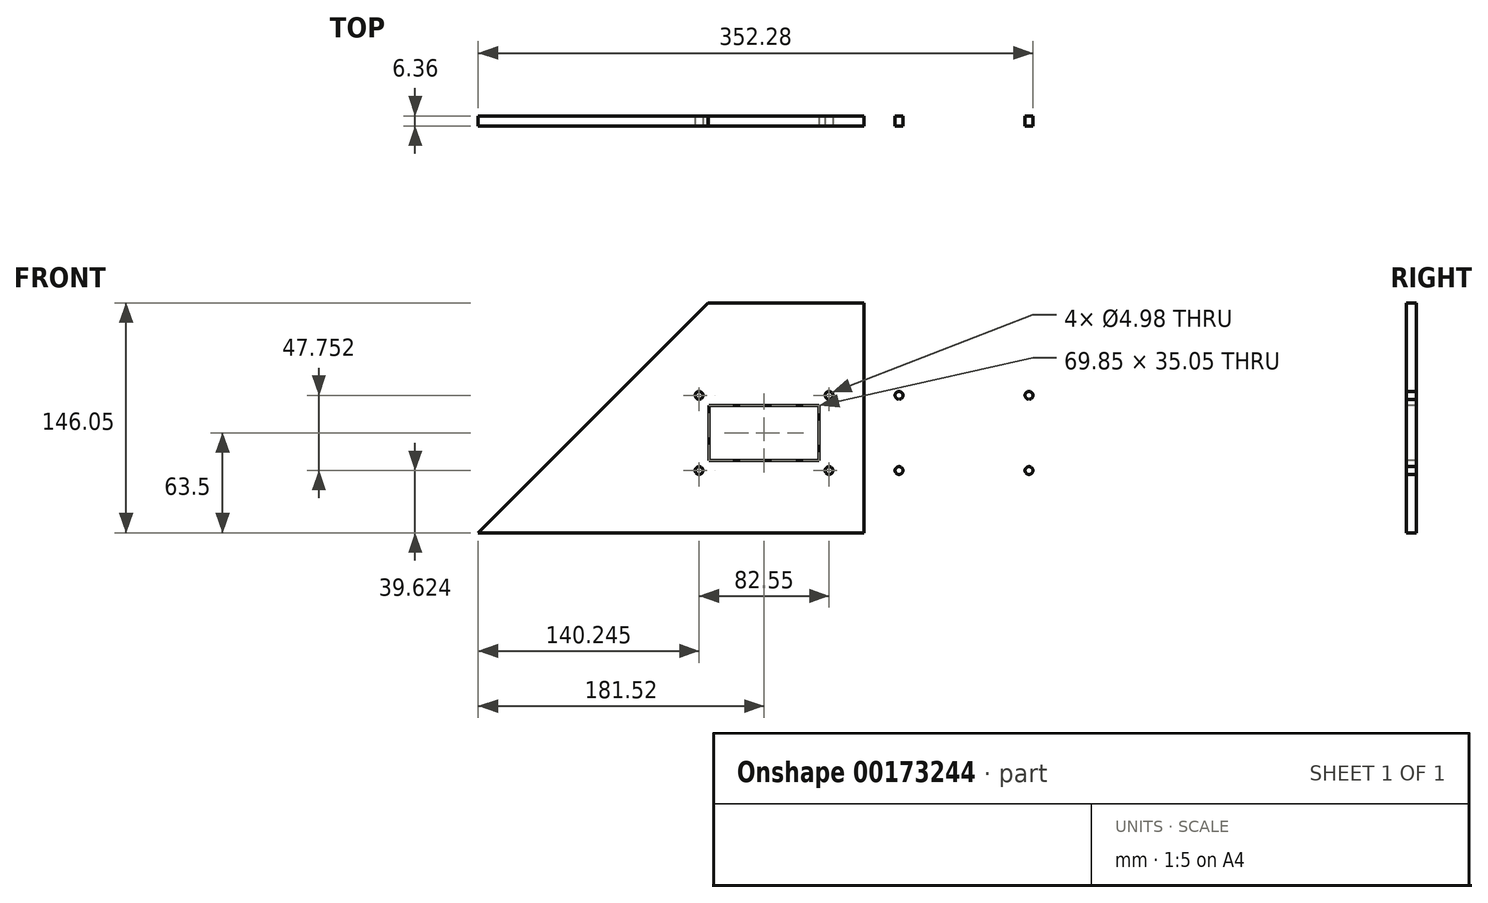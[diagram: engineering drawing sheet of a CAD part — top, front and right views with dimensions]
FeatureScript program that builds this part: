
annotation { "Feature Type Name" : "Feature", "Feature Type Description" : "" }
export const myFeature = defineFeature(function(context is Context, id is Id, definition is map)
    precondition{}
    {
        {
            var Q0;
            Q0=qCreatedBy(makeId("Front.planeOp"),FACE);
            var sketch = newSketch(context, id + "F0", { "sketchPlane" : qUnion([Q0])});
            skLineSegment(sketch, "E0", {"start": v(-98.97, 0) * mm, "end": v(98.97, 0) * mm});
            skLineSegment(sketch, "E1", {"start": v(-98.97, 0) * mm, "end": v(-245.02, -146.05) * mm});
            skLineSegment(sketch, "E2", {"start": v(-245.02, -146.05) * mm, "end": v(245.02, -146.05) * mm});
            skLineSegment(sketch, "E3", {"start": v(245.02, -146.05) * mm, "end": v(98.97, 0) * mm});
            skSolve(sketch);
        }
        {
            var Q0;
            Q0 = qSketchRegion(id + "F0", true);
            extrude(context, id + "F1", {"entities" : qUnion([Q0]), "endBound" : BoundingType.SYMMETRIC, "depth" : 6.35 * mm});
        }
        {
            var Q0;
            Q0=makeQuery(id+"F1.opExtrude","CAP_FACE",FACE,{"disambiguationData":[OSD([sQuery(id+"F0.wireOp",EDGE,"E0"),sQuery(id+"F0.wireOp",EDGE,"E1"),sQuery(id+"F0.wireOp",EDGE,"E2"),sQuery(id+"F0.wireOp",EDGE,"E3")])],"isStart":false});
            var sketch = newSketch(context, id + "F2", { "sketchPlane" : qUnion([Q0])});
            skLineSegment(sketch, "E4", {"start": v(0, 0) * mm, "end": v(0, -146.05) * mm});
            skPoint(sketch, "E5", {"position": v(-63.5, -82.55) * mm});
            skPoint(sketch, "E5.positionSnap0", {"position": v(0, -73.03) * mm});
            skLineSegment(sketch, "E6.bottom", {"start": v(-120.14, -45.09) * mm, "end": v(-6.86, -45.09) * mm});
            skLineSegment(sketch, "E6.top", {"start": v(-120.14, -120.02) * mm, "end": v(-6.86, -120.02) * mm});
            skLineSegment(sketch, "E6.left", {"start": v(-120.14, -45.09) * mm, "end": v(-120.14, -120.02) * mm});
            skLineSegment(sketch, "E6.right", {"start": v(-6.86, -45.09) * mm, "end": v(-6.86, -120.02) * mm});
            skLineSegment(sketch, "E7.bottom", {"start": v(-104.78, -58.67) * mm, "end": v(-22.23, -58.67) * mm});
            skLineSegment(sketch, "E7.top", {"start": v(-104.78, -106.43) * mm, "end": v(-22.23, -106.43) * mm});
            skLineSegment(sketch, "E7.left", {"start": v(-104.78, -58.67) * mm, "end": v(-104.78, -106.43) * mm});
            skLineSegment(sketch, "E7.right", {"start": v(-22.23, -58.67) * mm, "end": v(-22.23, -106.43) * mm});
            skLineSegment(sketch, "E8.bottom", {"start": v(-98.43, -65.02) * mm, "end": v(-28.58, -65.02) * mm});
            skLineSegment(sketch, "E8.top", {"start": v(-98.43, -100.08) * mm, "end": v(-28.58, -100.08) * mm});
            skLineSegment(sketch, "E8.left", {"start": v(-98.43, -65.02) * mm, "end": v(-98.43, -100.08) * mm});
            skLineSegment(sketch, "E8.right", {"start": v(-28.58, -65.02) * mm, "end": v(-28.58, -100.08) * mm});
            skCircle(sketch, "E9", {"center": v(-104.78, -58.67) * mm, "radius": 2.49 * mm});
            skCircle(sketch, "E10", {"center": v(-22.23, -58.67) * mm, "radius": 2.49 * mm});
            skCircle(sketch, "E11", {"center": v(-104.78, -106.43) * mm, "radius": 2.49 * mm});
            skCircle(sketch, "E12", {"center": v(-22.23, -106.43) * mm, "radius": 2.49 * mm});
            skLineSegment(sketch, "E13.MirrorCS", {"start": v(98.43, -65.02) * mm, "end": v(28.58, -65.02) * mm});
            skLineSegment(sketch, "E14.MirrorCS", {"start": v(98.43, -65.02) * mm, "end": v(98.43, -100.08) * mm});
            skLineSegment(sketch, "E15.MirrorCS", {"start": v(28.58, -65.02) * mm, "end": v(28.58, -100.08) * mm});
            skLineSegment(sketch, "E16.MirrorCS", {"start": v(98.43, -100.08) * mm, "end": v(28.58, -100.08) * mm});
            skCircle(sketch, "E17.MirrorC", {"center": v(104.78, -58.67) * mm, "radius": 2.49 * mm});
            skCircle(sketch, "E18.MirrorC", {"center": v(22.23, -58.67) * mm, "radius": 2.49 * mm});
            skCircle(sketch, "E19.MirrorC", {"center": v(22.23, -106.43) * mm, "radius": 2.49 * mm});
            skCircle(sketch, "E20.MirrorC", {"center": v(104.78, -106.43) * mm, "radius": 2.49 * mm});
            skSolve(sketch);
        }
        {
            var Q0;
            Q0=makeQuery(id+"F2.imprint","IMPRINT",FACE,{"disambiguationData":[TD([[makeQuery(id+"F2.imprint","IMPRINT",EDGE,{"derivedFrom":sQuery(id+"F2.wireOp",EDGE,"E13.MirrorCS")}),1.0]])]});
            var Q1;
            Q1=makeQuery(id+"F2.imprint","IMPRINT",FACE,{"disambiguationData":[TD([[makeQuery(id+"F2.imprint","IMPRINT",EDGE,{"derivedFrom":sQuery(id+"F2.wireOp",EDGE,"E17.MirrorC")}),-1.0]])]});
            var Q2;
            Q2=makeQuery(id+"F2.imprint","IMPRINT",FACE,{"disambiguationData":[TD([[makeQuery(id+"F2.imprint","IMPRINT",EDGE,{"derivedFrom":sQuery(id+"F2.wireOp",EDGE,"E18.MirrorC")}),-1.0]])]});
            var Q3;
            Q3=makeQuery(id+"F2.imprint","IMPRINT",FACE,{"disambiguationData":[TD([[makeQuery(id+"F2.imprint","IMPRINT",EDGE,{"derivedFrom":sQuery(id+"F2.wireOp",EDGE,"E19.MirrorC")}),-1.0]])]});
            var Q4;
            Q4=makeQuery(id+"F2.imprint","IMPRINT",FACE,{"disambiguationData":[TD([[makeQuery(id+"F2.imprint","IMPRINT",EDGE,{"derivedFrom":sQuery(id+"F2.wireOp",EDGE,"E20.MirrorC")}),-1.0]])]});
            var Q5;
            {var subQ0=sQuery(id+"F2.wireOp",EDGE,"E7.right");var subQ1=sQuery(id+"F2.wireOp",EDGE,"E7.bottom");var subQ2=makeQuery(id+"F2.imprint","INTERSECT",VERTEX,{"derivedFrom":[subQ1,subQ0]});Q5=makeQuery(id+"F2.imprint","IMPRINT",FACE,{"disambiguationData":[TD([[makeQuery(id+"F2.imprint","IMPRINT",EDGE,{"disambiguationData":[TD([[subQ2,1.0]])],"derivedFrom":subQ1}),1.0]])]});}
            var Q6;
            {var subQ0=sQuery(id+"F2.wireOp",EDGE,"E7.right");var subQ1=sQuery(id+"F2.wireOp",EDGE,"E7.bottom");var subQ2=makeQuery(id+"F2.imprint","INTERSECT",VERTEX,{"derivedFrom":[subQ1,subQ0]});Q6=makeQuery(id+"F2.imprint","IMPRINT",FACE,{"disambiguationData":[TD([[makeQuery(id+"F2.imprint","IMPRINT",EDGE,{"disambiguationData":[TD([[subQ2,1.0]])],"derivedFrom":subQ1}),-1.0]])]});}
            var Q7;
            {var subQ0=sQuery(id+"F2.wireOp",EDGE,"E7.right");var subQ1=sQuery(id+"F2.wireOp",EDGE,"E7.top");var subQ2=makeQuery(id+"F2.imprint","INTERSECT",VERTEX,{"derivedFrom":[subQ1,subQ0]});Q7=makeQuery(id+"F2.imprint","IMPRINT",FACE,{"disambiguationData":[TD([[makeQuery(id+"F2.imprint","IMPRINT",EDGE,{"disambiguationData":[TD([[subQ2,1.0]])],"derivedFrom":subQ1}),-1.0]])]});}
            var Q8;
            {var subQ0=sQuery(id+"F2.wireOp",EDGE,"E7.right");var subQ1=sQuery(id+"F2.wireOp",EDGE,"E7.top");var subQ2=makeQuery(id+"F2.imprint","INTERSECT",VERTEX,{"derivedFrom":[subQ1,subQ0]});Q8=makeQuery(id+"F2.imprint","IMPRINT",FACE,{"disambiguationData":[TD([[makeQuery(id+"F2.imprint","IMPRINT",EDGE,{"disambiguationData":[TD([[subQ2,1.0]])],"derivedFrom":subQ1}),1.0]])]});}
            var Q9;
            Q9=makeQuery(id+"F2.imprint","IMPRINT",FACE,{"disambiguationData":[TD([[makeQuery(id+"F2.imprint","IMPRINT",EDGE,{"derivedFrom":sQuery(id+"F2.wireOp",EDGE,"E8.bottom")}),-1.0]])]});
            var Q10;
            {var subQ0=sQuery(id+"F2.wireOp",EDGE,"E7.left");var subQ1=sQuery(id+"F2.wireOp",EDGE,"E7.bottom");var subQ2=makeQuery(id+"F2.imprint","INTERSECT",VERTEX,{"derivedFrom":[subQ1,subQ0]});Q10=makeQuery(id+"F2.imprint","IMPRINT",FACE,{"disambiguationData":[TD([[makeQuery(id+"F2.imprint","IMPRINT",EDGE,{"disambiguationData":[TD([[subQ2,-1.0]])],"derivedFrom":subQ1}),1.0]])]});}
            var Q11;
            {var subQ0=sQuery(id+"F2.wireOp",EDGE,"E7.left");var subQ1=sQuery(id+"F2.wireOp",EDGE,"E7.top");var subQ2=makeQuery(id+"F2.imprint","INTERSECT",VERTEX,{"derivedFrom":[subQ1,subQ0]});Q11=makeQuery(id+"F2.imprint","IMPRINT",FACE,{"disambiguationData":[TD([[makeQuery(id+"F2.imprint","IMPRINT",EDGE,{"disambiguationData":[TD([[subQ2,-1.0]])],"derivedFrom":subQ1}),-1.0]])]});}
            var Q12;
            {var subQ0=sQuery(id+"F2.wireOp",EDGE,"E7.left");var subQ1=sQuery(id+"F2.wireOp",EDGE,"E7.top");var subQ2=makeQuery(id+"F2.imprint","INTERSECT",VERTEX,{"derivedFrom":[subQ1,subQ0]});Q12=makeQuery(id+"F2.imprint","IMPRINT",FACE,{"disambiguationData":[TD([[makeQuery(id+"F2.imprint","IMPRINT",EDGE,{"disambiguationData":[TD([[subQ2,-1.0]])],"derivedFrom":subQ1}),1.0]])]});}
            var Q13;
            {var subQ0=sQuery(id+"F2.wireOp",EDGE,"E7.left");var subQ1=sQuery(id+"F2.wireOp",EDGE,"E7.bottom");var subQ2=makeQuery(id+"F2.imprint","INTERSECT",VERTEX,{"derivedFrom":[subQ1,subQ0]});Q13=makeQuery(id+"F2.imprint","IMPRINT",FACE,{"disambiguationData":[TD([[makeQuery(id+"F2.imprint","IMPRINT",EDGE,{"disambiguationData":[TD([[subQ2,-1.0]])],"derivedFrom":subQ1}),-1.0]])]});}
            extrude(context, id + "F3", {"entities" : qUnion([Q0, Q1, Q2, Q3, Q4, Q5, Q6, Q7, Q8, Q9, Q10, Q11, Q12, Q13]), "operationType" : NewBodyOperationType.REMOVE, "endBound" : BoundingType.THROUGH_ALL, "oppositeDirection" : true, "depth" : 25.4 * mm});
        }
    });
